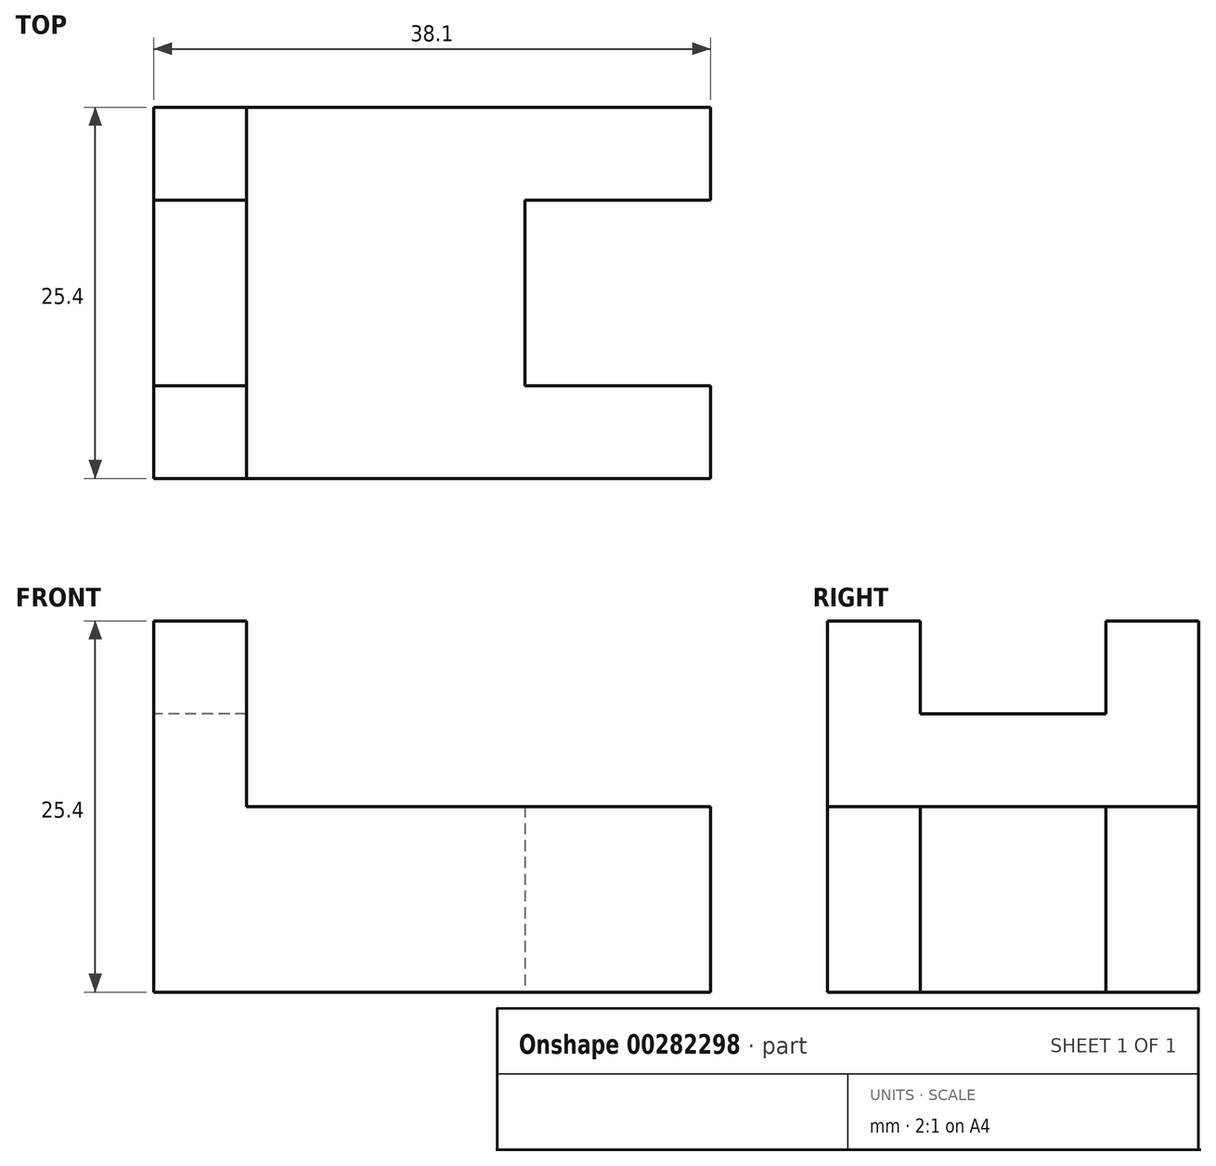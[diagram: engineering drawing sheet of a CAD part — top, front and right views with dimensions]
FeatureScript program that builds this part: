
annotation { "Feature Type Name" : "Feature", "Feature Type Description" : "" }
export const myFeature = defineFeature(function(context is Context, id is Id, definition is map)
    precondition{}
    {
        {
            var Q0;
            Q0=qCreatedBy(makeId("Top.planeOp"),FACE);
            var sketch = newSketch(context, id + "F0", { "sketchPlane" : qUnion([Q0])});
            skLineSegment(sketch, "E0", {"start": v(0, 0) * mm, "end": v(0, 25.4) * mm});
            skLineSegment(sketch, "E1", {"start": v(0, 25.4) * mm, "end": v(38.1, 25.4) * mm});
            skLineSegment(sketch, "E2", {"start": v(38.1, 25.4) * mm, "end": v(38.1, 19.05) * mm});
            skLineSegment(sketch, "E3", {"start": v(38.1, 19.05) * mm, "end": v(25.4, 19.05) * mm});
            skLineSegment(sketch, "E4", {"start": v(25.4, 19.05) * mm, "end": v(25.4, 6.35) * mm});
            skLineSegment(sketch, "E5", {"start": v(25.4, 6.35) * mm, "end": v(38.1, 6.35) * mm});
            skLineSegment(sketch, "E6", {"start": v(38.1, 6.35) * mm, "end": v(38.1, 0) * mm});
            skLineSegment(sketch, "E7", {"start": v(38.1, 0) * mm, "end": v(0, 0) * mm});
            skSolve(sketch);
        }
        {
            var Q0;
            Q0=makeQuery(id+"F0.imprint","IMPRINT",FACE,{"disambiguationData":[TD([[makeQuery(id+"F0.imprint","IMPRINT",EDGE,{"derivedFrom":sQuery(id+"F0.wireOp",EDGE,"E0")}),-1.0]])]});
            extrude(context, id + "F1", {"entities" : qUnion([Q0]), "depth" : 12.7 * mm});
        }
        {
            var Q0;
            Q0=qCreatedBy(makeId("Top.planeOp"),FACE);
            var sketch = newSketch(context, id + "F2", { "sketchPlane" : qUnion([Q0])});
            skLineSegment(sketch, "E8", {"start": v(0, 0) * mm, "end": v(0, 25.4) * mm});
            skLineSegment(sketch, "E9", {"start": v(0, 25.4) * mm, "end": v(6.35, 25.4) * mm});
            skLineSegment(sketch, "E10", {"start": v(6.35, 25.4) * mm, "end": v(6.35, 0) * mm});
            skLineSegment(sketch, "E11", {"start": v(6.35, 0) * mm, "end": v(0, 0) * mm});
            skSolve(sketch);
        }
        {
            var Q0;
            Q0 = qSketchRegion(id + "F2", true);
            extrude(context, id + "F3", {"entities" : qUnion([Q0]), "operationType" : NewBodyOperationType.ADD, "depth" : 25.4 * mm});
        }
        {
            var Q0;
            Q0=qCreatedBy(makeId("Right.planeOp"),FACE);
            var sketch = newSketch(context, id + "F4", { "sketchPlane" : qUnion([Q0])});
            skLineSegment(sketch, "E12.bottom", {"start": v(6.35, 25.4) * mm, "end": v(19.05, 25.4) * mm});
            skLineSegment(sketch, "E12.top", {"start": v(6.35, 19.05) * mm, "end": v(19.05, 19.05) * mm});
            skLineSegment(sketch, "E12.left", {"start": v(6.35, 25.4) * mm, "end": v(6.35, 19.05) * mm});
            skLineSegment(sketch, "E12.right", {"start": v(19.05, 25.4) * mm, "end": v(19.05, 19.05) * mm});
            skSolve(sketch);
        }
        {
            var Q0;
            Q0 = qSketchRegion(id + "F4", true);
            extrude(context, id + "F5", {"entities" : qUnion([Q0]), "operationType" : NewBodyOperationType.REMOVE, "depth" : 25.4 * mm});
        }
    });
